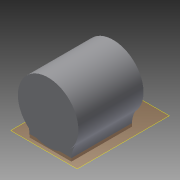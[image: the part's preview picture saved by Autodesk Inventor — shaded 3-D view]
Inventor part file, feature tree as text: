
AUTODESK INVENTOR PART (.ipt)
format: ipt  version: 2015 SP1 (Build 190203100, 203)  size: 130,048 bytes
history: native  units: in
note: dims shown in document units (in); Inventor stores cm internally (conversion verified against a paired STEP export)
features: sketch x4, extrude x3, fillet x2, hole x1, plane x1, projected_geometry x1
ambient origin geometry x8: Origin, YZ Plane, XZ Plane, XY Plane, X Axis, Y Axis, Z Axis, Center Point
bodies: Solid1 (feature_tree)
feature tree (12):
  extrude  "Extrusion1"  Depth=0.1in
  extrude  "Extrusion2"  Depth=2.0in
  hole  "Hole1"  [1 undecoded]
  plane  "Work Plane1"
  extrude  "Extrusion3"  TaperAngle=0.0deg  [1 undecoded]
  fillet  "Fillet1"  Radius=5.75in
  fillet  "Fillet2"  [1 undecoded]
  sketch  "Sketch1"  dims[d0=0.625in d1=0.1in]
  sketch  "Sketch2"  dims[d2=0.191in d3=2.0in]
  sketch  "Sketch3"  dims[d4=0.0in d5=6.5in]
  sketch  "Sketch4"  dims[d6=7.0in d7=0.0in d8=5.75in d9=45.0deg d10=45.0deg d11=135.0deg d12=135.0deg d13=0.196in d14=0.5in d15=0.375in d16=0.25in d17=0.5635in d18=0.75in d19=0.8108in d20=6.5in d21=0.25in d22=4.5in d23=1.0in d24=0.0in d25=3.0in d26=3.0in d27=0.331in d28=0.0in]
  projected_geometry  "Projected Loop1"
note: 3 required parameter values undecoded (feature->parameter linkage not recoverable at this tier; creation-order binding heuristic only, values carry confidence <= 0.55)
